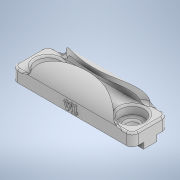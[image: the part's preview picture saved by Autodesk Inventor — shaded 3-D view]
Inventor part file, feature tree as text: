
AUTODESK INVENTOR PART (.ipt)
format: ipt  version: 2020 (Build 240168000, 168)  size: 353,792 bytes
history: native  units: in
note: dims shown in document units (in); Inventor stores cm internally (conversion verified against a paired STEP export)
features: sketch x6, extrude x4, fillet x3, hole x1, emboss x1
ambient origin geometry x8: Origin, YZ Plane, XZ Plane, XY Plane, X Axis, Y Axis, Z Axis, Center Point
bodies: Solid1 (feature_tree)
feature tree (15):
  extrude  "Extrusion1"  Depth=0.6in
  extrude  "Extrusion2"  Depth=0.11in
  hole  "Hole1"  [1 undecoded]
  extrude  "Extrusion3"  Depth=0.3in
  extrude  "Extrusion4"  Depth=0.05in
  fillet  "Fillet2"  Radius=0.1in
  emboss  "Emboss1"
  fillet  "Fillet3"  Radius=0.3in
  fillet  "Fillet4"  Radius=0.07in
  sketch  "Sketch1"  dims[d0=2.0in d1=0.6in]
  sketch  "Sketch2"  dims[d2=0.2in d3=0.0in d4=0.11in]
  sketch  "Sketch3"  dims[d5=0.11in d6=0.1in d7=0.0in]
  sketch  "Sketch4"  dims[d8=0.3in d9=0.3in]
  sketch  "Sketch5"  dims[d10=0.2in d11=0.75in d12=0.4in d13=0.15in d14=0.5635in d15=1.0in d16=0.8108in d17=0.05in d18=0.1in d19=0.3in d20=0.0in d22=0.07in]
  sketch  "Sketch6"  dims[d23=0.07in d24=0.07in d25=2.0in d26=0.0in d27=0.1in d28=0.03in d29=0.0in d30=0.03in d31=0.05in]
note: 1 required parameter value undecoded (feature->parameter linkage not recoverable at this tier; creation-order binding heuristic only, values carry confidence <= 0.55)
